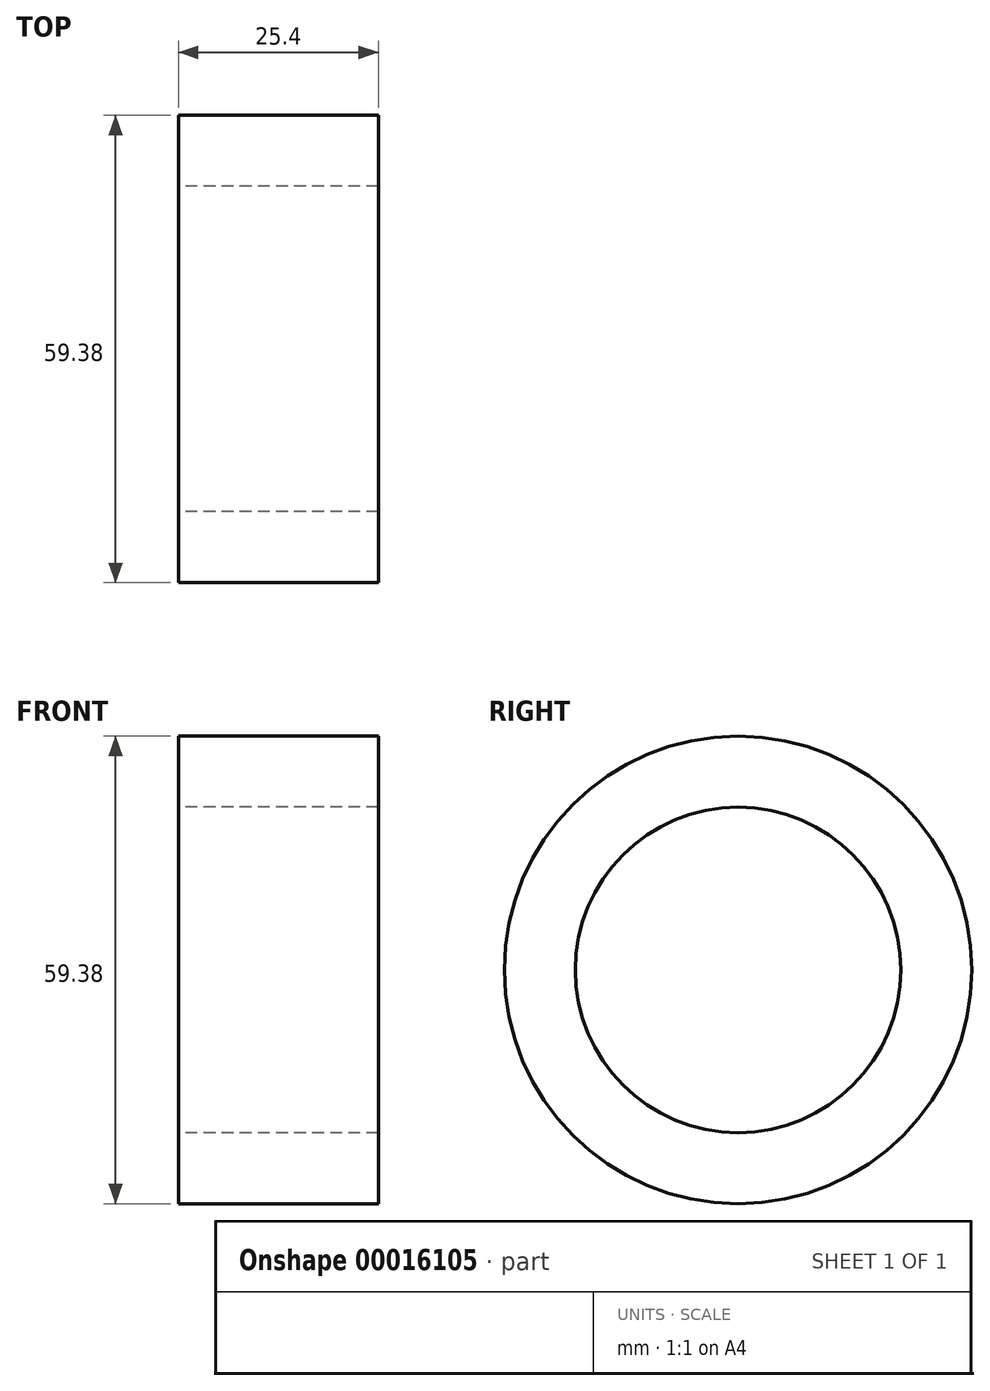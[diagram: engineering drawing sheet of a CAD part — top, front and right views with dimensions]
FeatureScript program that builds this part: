
annotation { "Feature Type Name" : "Feature", "Feature Type Description" : "" }
export const myFeature = defineFeature(function(context is Context, id is Id, definition is map)
    precondition{}
    {
        {
            var Q0;
            Q0=qCreatedBy(makeId("Right.planeOp"),FACE);
            var sketch = newSketch(context, id + "F0", { "sketchPlane" : qUnion([Q0])});
            skCircle(sketch, "E0", {"center": v(0, 0) * mm, "radius": 29.7 * mm});
            skCircle(sketch, "E1", {"center": v(0, 0) * mm, "radius": 20.68 * mm});
            skLineSegment(sketch, "E2", {"start": v(0, 0) * mm, "end": v(-20.68, 0) * mm});
            skSolve(sketch);
        }
        {
            var Q0;
            Q0=makeQuery(id+"F0.imprint","IMPRINT",FACE,{"disambiguationData":[TD([[makeQuery(id+"F0.imprint","IMPRINT",EDGE,{"derivedFrom":sQuery(id+"F0.wireOp",EDGE,"E0")}),1.0]])]});
            extrude(context, id + "F1", {"entities" : qUnion([Q0]), "depth" : 25.4 * mm});
        }
    });
